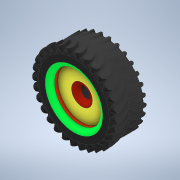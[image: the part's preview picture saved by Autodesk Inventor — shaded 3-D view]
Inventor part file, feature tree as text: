
AUTODESK INVENTOR PART (.ipt)
format: ipt  version: 2021.3 (Build 253353000, 353)  size: 970,240 bytes
history: native  units: mm
features: extrude x4, sketch x4, fillet x3, plane x1, pattern_circular x1
ambient origin geometry x8: Origin, YZ Plane, XZ Plane, XY Plane, X Axis, Y Axis, Z Axis, Center Point
bodies: Solid1 (feature_tree)
feature tree (13):
  extrude  "Extrusion1"  Depth=20.0mm TaperAngle=0.0deg
  fillet  "Fillet1"  Radius=3.0mm
  plane  "Work Plane1"
  extrude  "Extrusion2"  Depth=26.0mm
  pattern_circular  "Circular Pattern1"  Count=30 Angle=360.0deg
  extrude  "Extrusion3"  Depth=3.0mm
  extrude  "Extrusion4"  Depth=3.0mm
  fillet  "Fillet2"  Radius=5.0mm
  fillet  "Fillet3"  Radius=30.0mm
  sketch  "Sketch1"  dims[d0=50.0mm d1=20.0mm d2=0.0mm d3=3.0mm]
  sketch  "Sketch3"  dims[d4=25.0mm d5=26.0mm]
  sketch  "Sketch4"  dims[d6=10.0mm]
  sketch  "Sketch5"  dims[d7=5.0mm d8=0.0mm d9=300.0mm d10=360.0deg d12=35.0mm d13=7.0mm d14=5.0mm d15=0.0mm d16=30.0mm d17=5.0mm d18=0.0mm d19=3.0mm d20=3.0mm]
